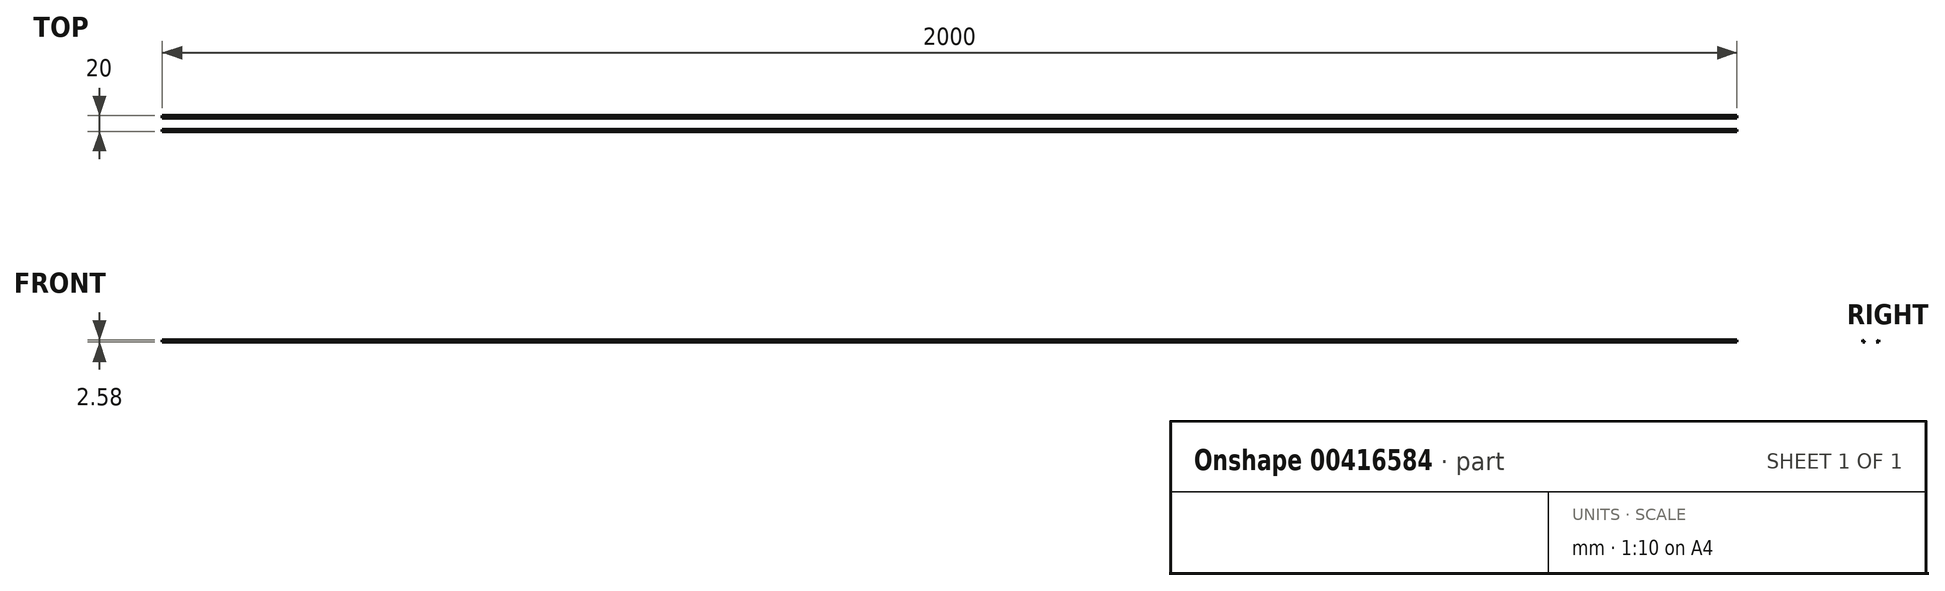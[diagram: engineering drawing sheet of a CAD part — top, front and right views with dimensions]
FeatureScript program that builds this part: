
annotation { "Feature Type Name" : "Feature", "Feature Type Description" : "" }
export const myFeature = defineFeature(function(context is Context, id is Id, definition is map)
    precondition{}
    {
        {
            assignVariable(context, id + "F0", {"name" : "l", "anyValue" : 2000});
        }
        {
            var Q0;
            Q0=qCreatedBy(makeId("Right.planeOp"),FACE);
            var sketch = newSketch(context, id + "F1", { "sketchPlane" : qUnion([Q0])});
            skLineSegment(sketch, "E0.bottom", {"start": v(-10, -10) * mm, "end": v(10, -10) * mm});
            skLineSegment(sketch, "E0.top", {"start": v(-10, 10) * mm, "end": v(10, 10) * mm});
            skLineSegment(sketch, "E0.left", {"start": v(-10, -10) * mm, "end": v(-10, 10) * mm});
            skLineSegment(sketch, "E0.right", {"start": v(10, -10) * mm, "end": v(10, 10) * mm});
            skPoint(sketch, "E0.middle", {"position": v(0, 0) * mm});
            skCircle(sketch, "E1", {"center": v(0, 0) * mm, "radius": 12.45 * mm});
            skLineSegment(sketch, "E2.0", {"start": v(-8.5, 8.5) * mm, "end": v(8.5, 8.5) * mm});
            skLineSegment(sketch, "E2.1", {"start": v(-8.5, -8.5) * mm, "end": v(-8.5, 8.5) * mm});
            skLineSegment(sketch, "E2.2", {"start": v(-8.5, -8.5) * mm, "end": v(8.5, -8.5) * mm});
            skLineSegment(sketch, "E2.3", {"start": v(8.5, -8.5) * mm, "end": v(8.5, 8.5) * mm});
            skLineSegment(sketch, "E3", {"start": v(-10, 10) * mm, "end": v(-8.5, 8.5) * mm});
            skSolve(sketch);
        }
        {
            var Q0;
            Q0=makeQuery(id+"F1.imprint","IMPRINT",FACE,{"disambiguationData":[TD([[makeQuery(id+"F1.imprint","IMPRINT",EDGE,{"derivedFrom":sQuery(id+"F1.wireOp",EDGE,"E0.bottom")}),1.0]])]});
            extrude(context, id + "F2", {"entities" : qUnion([Q0]), "depth" : getVariable(context, 'l') * mm, "offsetDistance" : 25 * mm});
        }
    });
